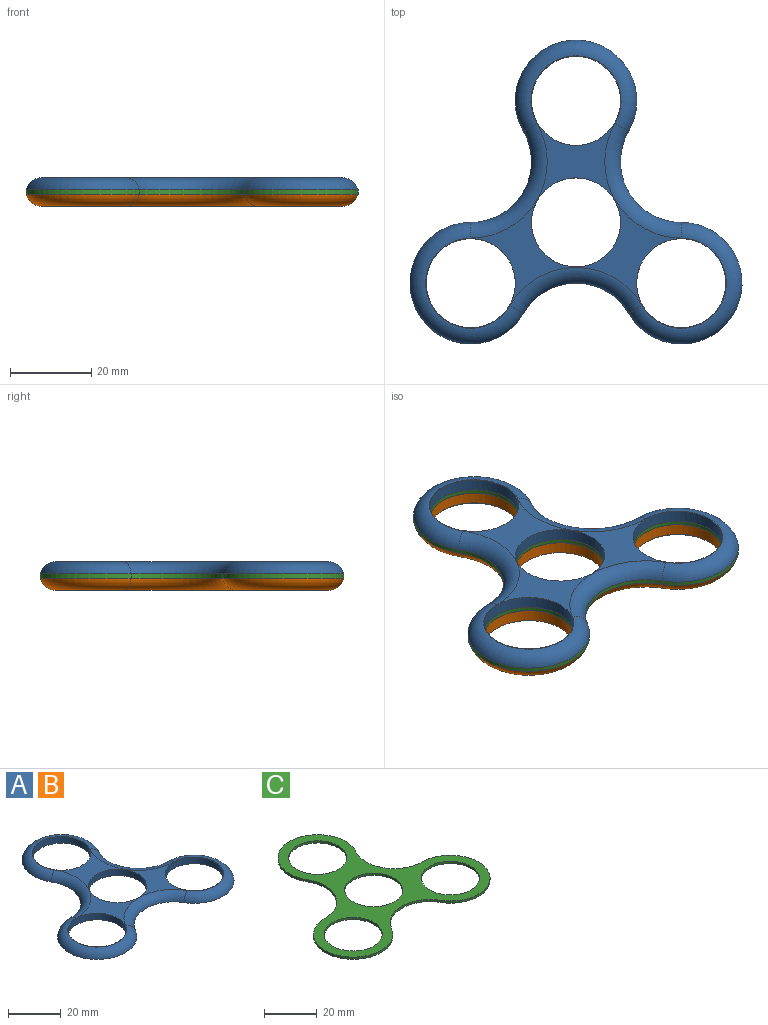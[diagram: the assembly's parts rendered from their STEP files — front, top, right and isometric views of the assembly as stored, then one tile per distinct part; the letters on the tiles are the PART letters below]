
ASSEMBLY  parts=3 mates=1
PART A: 12 faces, bbox 84.7x77.7x4 mm
  f0: cylinder r=11mm len=22mm, axis (0,0,-1), area 207.3mm2, adj f4,f5
  f1: cylinder r=11mm len=22mm, axis (0,0,-1), area 207.3mm2, adj f4,f5
  f2: cylinder r=11mm len=22mm, axis (0,0,-1), area 207.3mm2, adj f4,f5
  f3: cylinder r=11mm len=22mm, axis (0,0,-1), area 207.3mm2, adj f4,f5
  f4: plane 74.22x67.25mm, normal (0,0,1), area 476.7mm2, adj f0,f1,f2,f3,f6,f7,f8,f9
  f5: plane 81.96x75mm, normal (0,0,-1), area 1524.6mm2, adj f0,f1,f2,f3,f6,f7,f8,f9
  f6: torus R=18.87mm, axis (0,0,1), area 183.3mm2, adj f4,f5,f7,f8
  f7: torus R=11.13mm, axis (0,0,-1), area 296mm2, adj f4,f5,f6,f9
  f8: torus R=11.13mm, axis (0,0,-1), area 296mm2, adj f4,f5,f6,f10
  f9: torus R=18.87mm, axis (0,0,1), area 183.3mm2, adj f4,f5,f7,f11
  f10: torus R=18.87mm, axis (0,0,1), area 183.3mm2, adj f4,f5,f8,f11
  f11: torus R=11.13mm, axis (0,0,-1), area 296mm2, adj f4,f5,f9,f10
PART B: same geometry as A
PART C: 12 faces, bbox 82x75x1 mm
  f0: cylinder r=15mm len=30mm, axis (0,0,-1), area 62.8mm2, adj f1,f7,f10,f11
  f1: cylinder r=15mm len=25.98mm, axis (0,0,-1), area 31.4mm2, adj f0,f2,f10,f11
  f2: cylinder r=15mm len=30mm, axis (0,0,-1), area 62.8mm2, adj f1,f3,f10,f11
  f3: cylinder r=15mm len=22.5mm, axis (0,0,-1), area 31.4mm2, adj f2,f4,f10,f11
  f4: cylinder r=15mm len=30mm, axis (0,0,-1), area 62.8mm2, adj f3,f7,f10,f11
  f5: cylinder r=11mm len=22mm, axis (0,0,-1), area 69.1mm2, adj f10,f11
  f6: cylinder r=11mm len=22mm, axis (0,0,-1), area 69.1mm2, adj f10,f11
  f7: cylinder r=15mm len=22.5mm, axis (0,0,-1), area 31.4mm2, adj f0,f4,f10,f11
  f8: cylinder r=11mm len=22mm, axis (0,0,-1), area 69.1mm2, adj f10,f11
  f9: cylinder r=11mm len=22mm, axis (0,0,-1), area 69.1mm2, adj f10,f11
  f10: plane 81.96x75mm, normal (0,0,1), area 1524.6mm2, adj f0,f1,f2,f3,f4,f5,f6,f7
  f11: plane 81.96x75mm, normal (0,0,-1), area 1524.6mm2, adj f0,f1,f2,f3,f4,f5,f6,f7
PLACE A t=(1.67,-1.66,6.81)mm
PLACE B rot(axis=(0,1,0),180deg) t=(1.67,-1.66,5.81)mm
PLACE C t=(1.67,-1.66,5.81)mm
MATE fastened B.f1 <-> C.f6  axis (0,0,1) through (1.67,-1.66,5.81)mm
